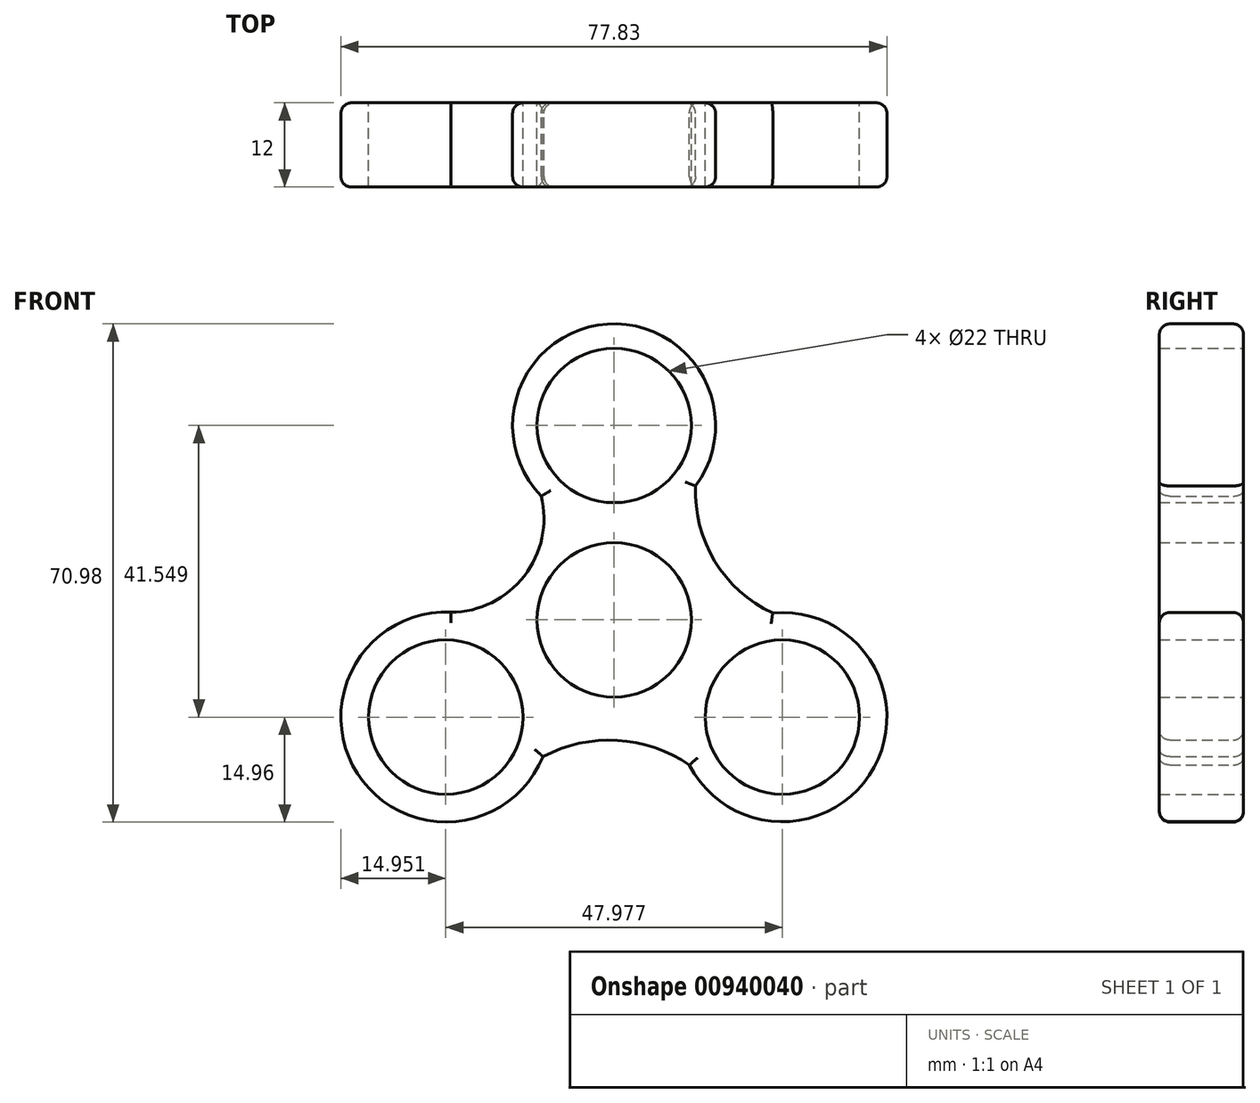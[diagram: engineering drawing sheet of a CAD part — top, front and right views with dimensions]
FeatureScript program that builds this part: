
annotation { "Feature Type Name" : "Feature", "Feature Type Description" : "" }
export const myFeature = defineFeature(function(context is Context, id is Id, definition is map)
    precondition{}
    {
        {
            var Q0;
            Q0=qCreatedBy(makeId("Front.planeOp"),FACE);
            var sketch = newSketch(context, id + "F0", { "sketchPlane" : qUnion([Q0])});
            skCircle(sketch, "E0", {"center": v(0, 0) * mm, "radius": 11 * mm});
            skCircle(sketch, "E1", {"center": v(0, 27.7) * mm, "radius": 11 * mm});
            skCircle(sketch, "E2.1.0", {"center": v(-23.99, -13.85) * mm, "radius": 11 * mm});
            skCircle(sketch, "E2.2.0", {"center": v(23.99, -13.85) * mm, "radius": 11 * mm});
            skCircle(sketch, "E3", {"center": v(0, 27.7) * mm, "radius": 14.47 * mm});
            skCircle(sketch, "E4", {"center": v(23.99, -13.85) * mm, "radius": 14.9 * mm});
            skCircle(sketch, "E5", {"center": v(-23.99, -13.85) * mm, "radius": 14.96 * mm});
            skArc(sketch, "E6", {"start": v(-24.04, 1.1) * mm, "mid": v(-13.05, 5.93) * mm, "end": v(-10.4, 17.64) * mm});
            skArc(sketch, "E7", {"start": v(11.62, 19.09) * mm, "mid": v(14.36, 8.36) * mm, "end": v(22.63, 1) * mm});
            skArc(sketch, "E8", {"start": v(10.74, -20.68) * mm, "mid": v(0.47, -17.17) * mm, "end": v(-10.13, -19.48) * mm});
            skSolve(sketch);
        }
        {
            var Q0;
            Q0 = qSketchRegion(id + "F0", true);
            extrude(context, id + "F1", {"entities" : qUnion([Q0]), "depth" : 12 * mm, "offsetDistance" : 25 * mm});
        }
        {
            var Q0;
            Q0=makeQuery(id+"F1.opExtrude","CAP_EDGE",EDGE,{"disambiguationData":[OSD([sQuery(id+"F0.wireOp",EDGE,"E3")])],"isStart":false});
            var Q1;
            Q1=makeQuery(id+"F1.opExtrude","CAP_EDGE",EDGE,{"disambiguationData":[OSD([sQuery(id+"F0.wireOp",EDGE,"E6")])],"isStart":false});
            var Q2;
            Q2=makeQuery(id+"F1.opExtrude","CAP_EDGE",EDGE,{"disambiguationData":[OSD([sQuery(id+"F0.wireOp",EDGE,"E5")])],"isStart":false});
            var Q3;
            Q3=makeQuery(id+"F1.opExtrude","CAP_EDGE",EDGE,{"disambiguationData":[OSD([sQuery(id+"F0.wireOp",EDGE,"E7")])],"isStart":false});
            var Q4;
            Q4=makeQuery(id+"F1.opExtrude","CAP_EDGE",EDGE,{"disambiguationData":[OSD([sQuery(id+"F0.wireOp",EDGE,"E4")])],"isStart":false});
            var Q5;
            Q5=makeQuery(id+"F1.opExtrude","CAP_EDGE",EDGE,{"disambiguationData":[OSD([sQuery(id+"F0.wireOp",EDGE,"E8")])],"isStart":false});
            fillet(context, id + "F2", {"entities" : qUnion([Q0, Q1, Q2, Q3, Q4, Q5]), "radius" : 1.5 * mm, "tangentPropagation" : true, "allowEdgeOverflow" : false});
        }
        {
            var Q0;
            Q0=makeQuery(id+"F1.opExtrude","CAP_EDGE",EDGE,{"disambiguationData":[OSD([sQuery(id+"F0.wireOp",EDGE,"E4")])],"isStart":true});
            var Q1;
            Q1=makeQuery(id+"F1.opExtrude","CAP_EDGE",EDGE,{"disambiguationData":[OSD([sQuery(id+"F0.wireOp",EDGE,"E8")])],"isStart":true});
            var Q2;
            Q2=makeQuery(id+"F1.opExtrude","CAP_EDGE",EDGE,{"disambiguationData":[OSD([sQuery(id+"F0.wireOp",EDGE,"E5")])],"isStart":true});
            var Q3;
            Q3=makeQuery(id+"F1.opExtrude","CAP_EDGE",EDGE,{"disambiguationData":[OSD([sQuery(id+"F0.wireOp",EDGE,"E6")])],"isStart":true});
            var Q4;
            Q4=makeQuery(id+"F1.opExtrude","CAP_EDGE",EDGE,{"disambiguationData":[OSD([sQuery(id+"F0.wireOp",EDGE,"E3")])],"isStart":true});
            var Q5;
            Q5=makeQuery(id+"F1.opExtrude","CAP_EDGE",EDGE,{"disambiguationData":[OSD([sQuery(id+"F0.wireOp",EDGE,"E7")])],"isStart":true});
            fillet(context, id + "F3", {"entities" : qUnion([Q0, Q1, Q2, Q3, Q4, Q5]), "radius" : 1.5 * mm, "tangentPropagation" : true, "allowEdgeOverflow" : false});
        }
    });
